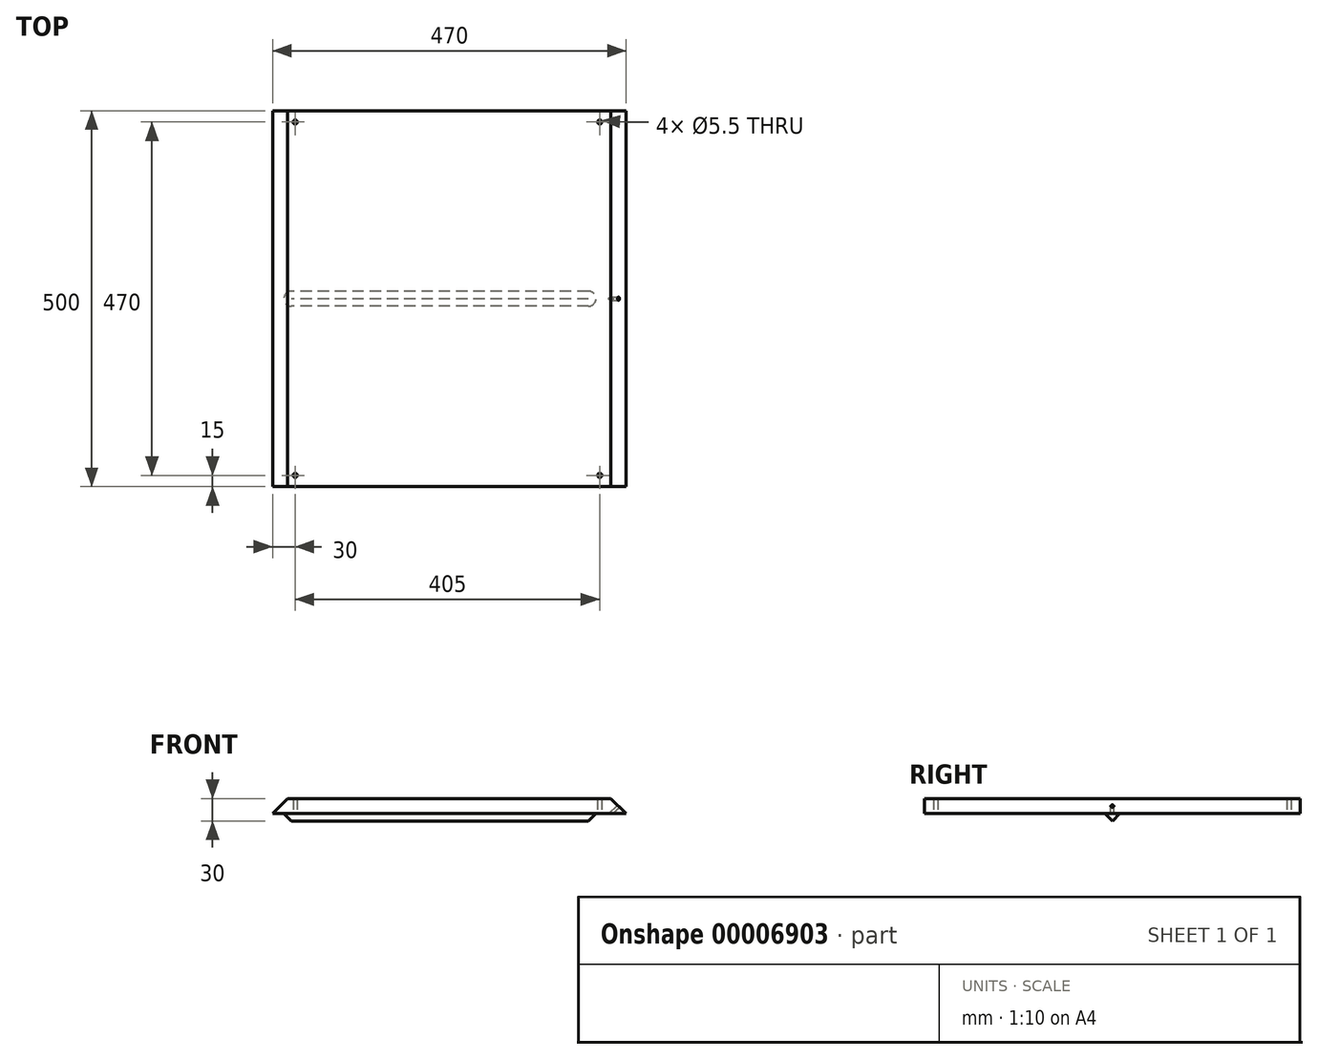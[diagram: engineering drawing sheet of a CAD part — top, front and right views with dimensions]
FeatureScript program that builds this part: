
annotation { "Feature Type Name" : "Feature", "Feature Type Description" : "" }
export const myFeature = defineFeature(function(context is Context, id is Id, definition is map)
    precondition{}
    {
        {
            var Q0;
            Q0=qCreatedBy(makeId("Top.planeOp"),FACE);
            var sketch = newSketch(context, id + "F0", { "sketchPlane" : qUnion([Q0])});
            skLineSegment(sketch, "E0.rect.bottom", {"start": v(242.5, -250) * mm, "end": v(-242.5, -250) * mm});
            skLineSegment(sketch, "E0.rect.top", {"start": v(242.5, 250) * mm, "end": v(-242.5, 250) * mm});
            skLineSegment(sketch, "E0.rect.left", {"start": v(242.5, -250) * mm, "end": v(242.5, 250) * mm});
            skLineSegment(sketch, "E0.rect.right", {"start": v(-242.5, -250) * mm, "end": v(-242.5, 250) * mm});
            skPoint(sketch, "E0.rect.middle", {"position": v(0, 0) * mm});
            skLineSegment(sketch, "E1", {"start": v(-242.5, 0) * mm, "end": v(242.5, 0) * mm, "construction": true});
            skCircle(sketch, "E2", {"center": v(-212.5, 235) * mm, "radius": 2.75 * mm});
            skCircle(sketch, "E3", {"center": v(-212.5, -235) * mm, "radius": 2.75 * mm});
            skCircle(sketch, "E4", {"center": v(192.5, 235) * mm, "radius": 2.75 * mm});
            skCircle(sketch, "E5", {"center": v(192.5, -235) * mm, "radius": 2.75 * mm});
            skSolve(sketch);
        }
        {
            var Q0;
            Q0=qSketchRegion(id+"F0",true);
            var Q1;
            Q1=makeQuery(id+"F0.imprint","IMPRINT",FACE,{"disambiguationData":[TD([[makeQuery(id+"F0.imprint","IMPRINT",EDGE,{"derivedFrom":sQuery(id+"F0.wireOp",EDGE,"E0.rect.bottom")}),-1.0]])]});
            extrude(context, id + "F1", {"entities" : qUnion([Q0, Q1]), "depth" : (30) * mm});
        }
        {
            var Q0;
            Q0=makeQuery(id+"F1.opExtrude","SWEPT_FACE",FACE,{"disambiguationData":[OSD([sQuery(id+"F0.wireOp",EDGE,"E0.rect.right")])]});
            var sketch = newSketch(context, id + "F2", { "sketchPlane" : qUnion([Q0])});
            skLineSegment(sketch, "E6", {"start": v(0, 0) * mm, "end": v(-10, 10) * mm});
            skLineSegment(sketch, "E7", {"start": v(0, 0) * mm, "end": v(10, 10) * mm});
            skLineSegment(sketch, "E8", {"start": v(-10, 10) * mm, "end": v(-250, 10) * mm});
            skLineSegment(sketch, "E9", {"start": v(10, 10) * mm, "end": v(250, 10) * mm});
            skSolve(sketch);
        }
        {
            var Q0;
            Q0=qSketchRegion(id+"F2",true);
            var Q1;
            {var subQ2=sQuery(id+"F2.wireOp",EDGE,"E6");Q1=makeQuery(id+"F2.imprint","IMPRINT",FACE,{"disambiguationData":[TD([[makeQuery(id+"F2.imprint","IMPRINT",EDGE,{"derivedFrom":subQ2}),1.0]])]});}
            var Q2;
            {var subQ2=sQuery(id+"F2.wireOp",EDGE,"E7");Q2=makeQuery(id+"F2.imprint","IMPRINT",FACE,{"disambiguationData":[TD([[makeQuery(id+"F2.imprint","IMPRINT",EDGE,{"derivedFrom":subQ2}),-1.0]])]});}
            extrude(context, id + "F3", {"entities" : qUnion([Q0, Q1, Q2]), "operationType" : NewBodyOperationType.REMOVE, "endBound" : BoundingType.THROUGH_ALL, "oppositeDirection" : true, "depth" : 25 * mm});
        }
        {
            var Q0;
            Q0=makeQuery(id+"F1.opExtrude","SWEPT_FACE",FACE,{"disambiguationData":[OSD([sQuery(id+"F0.wireOp",EDGE,"E0.rect.right")])]});
            var sketch = newSketch(context, id + "F4", { "sketchPlane" : qUnion([Q0])});
            skLineSegment(sketch, "E10", {"start": v(-10, 10) * mm, "end": v(10, 10) * mm});
            skSolve(sketch);
        }
        {
            var Q0;
            Q0=qSketchRegion(id+"F4",true);
            var Q1;
            Q1=makeQuery(id+"F4.imprint","IMPRINT",FACE,{"disambiguationData":[TD([[makeQuery(id+"F4.imprint","IMPRINT",EDGE,{"derivedFrom":sQuery(id+"F4.wireOp",EDGE,"E10")}),-1.0]])]});
            extrude(context, id + "F5", {"entities" : qUnion([Q0, Q1]), "operationType" : NewBodyOperationType.REMOVE, "oppositeDirection" : true, "depth" : 25 * mm});
        }
        {
            var Q0;
            Q0=makeQuery(id+"F5.boolean.opBoolean","COPY",FACE,{"derivedFrom":makeQuery(id+"F5.opExtrude","CAP_FACE",FACE,{"disambiguationData":[OSD([sQuery(id+"F2.wireOp",EDGE,"E6"),sQuery(id+"F2.wireOp",EDGE,"E7"),sQuery(id+"F4.wireOp",EDGE,"E10")])],"isStart":false})});
            var sketch = newSketch(context, id + "F6", { "sketchPlane" : qUnion([Q0])});
            skLineSegment(sketch, "E11", {"start": v(0, 0) * mm, "end": v(0, 10) * mm});
            skSolve(sketch);
        }
        {
            var Q0;
            {var subQ1=sQuery(id+"F6.wireOp",EDGE,"E11");Q0=makeQuery(id+"F6.imprint","IMPRINT",FACE,{"disambiguationData":[TD([[makeQuery(id+"F6.imprint","IMPRINT",EDGE,{"derivedFrom":subQ1}),1.0]])]});}
            var Q1;
            Q1=sQuery(id+"F6.wireOp",EDGE,"E11");
            revolve(context, id + "F7", {"operationType" : NewBodyOperationType.ADD, "entities" : qUnion([Q0]), "axis" : qUnion([Q1]), "revolveType" : RevolveType.FULL});
        }
        {
            var Q0;
            Q0=makeQuery(id+"F1.opExtrude","SWEPT_FACE",FACE,{"disambiguationData":[OSD([sQuery(id+"F0.wireOp",EDGE,"E0.rect.top")])]});
            var sketch = newSketch(context, id + "F8", { "sketchPlane" : qUnion([Q0])});
            skLineSegment(sketch, "E12", {"start": v(242.5, 10) * mm, "end": v(222.5, 30) * mm});
            skSolve(sketch);
        }
        {
            var Q0;
            Q0=qSketchRegion(id+"F8",true);
            var Q1;
            {var subQ2=sQuery(id+"F8.wireOp",EDGE,"E12");Q1=makeQuery(id+"F8.imprint","IMPRINT",FACE,{"disambiguationData":[TD([[makeQuery(id+"F8.imprint","IMPRINT",EDGE,{"derivedFrom":subQ2}),-1.0]])]});}
            extrude(context, id + "F9", {"entities" : qUnion([Q0, Q1]), "operationType" : NewBodyOperationType.REMOVE, "endBound" : BoundingType.THROUGH_ALL, "oppositeDirection" : true, "depth" : 25 * mm});
        }
        {
            var Q0;
            Q0=makeQuery(id+"F1.opExtrude","SWEPT_FACE",FACE,{"disambiguationData":[OSD([sQuery(id+"F0.wireOp",EDGE,"E0.rect.left")])]});
            extrude(context, id + "F10", {"entities" : qUnion([Q0]), "operationType" : NewBodyOperationType.REMOVE, "oppositeDirection" : true, "depth" : (15) * mm});
        }
        {
            var Q0;
            Q0=makeQuery(id+"F10.boolean.opBoolean","COPY",FACE,{"derivedFrom":makeQuery(id+"F10.opExtrude","CAP_FACE",FACE,{"disambiguationData":[OSD([sQuery(id+"F0.wireOp",EDGE,"E0.rect.left")])],"isStart":false})});
            var sketch = newSketch(context, id + "F11", { "sketchPlane" : qUnion([Q0])});
            skLineSegment(sketch, "E13", {"start": v(-10, 10) * mm, "end": v(10, 10) * mm});
            skSolve(sketch);
        }
        {
            var Q0;
            Q0=makeQuery(id+"F11.imprint","IMPRINT",FACE,{"disambiguationData":[TD([[makeQuery(id+"F11.imprint","IMPRINT",EDGE,{"derivedFrom":sQuery(id+"F11.wireOp",EDGE,"E13")}),-1.0]])]});
            extrude(context, id + "F12", {"entities" : qUnion([Q0]), "operationType" : NewBodyOperationType.REMOVE, "oppositeDirection" : true, "depth" : (50) * mm});
        }
        {
            var Q0;
            Q0=makeQuery(id+"F12.boolean.opBoolean","COPY",FACE,{"derivedFrom":makeQuery(id+"F12.opExtrude","CAP_FACE",FACE,{"disambiguationData":[OSD([sQuery(id+"F0.wireOp",EDGE,"E0.rect.left"),sQuery(id+"F2.wireOp",EDGE,"E6"),sQuery(id+"F2.wireOp",EDGE,"E7"),sQuery(id+"F11.wireOp",EDGE,"E13")])],"isStart":false})});
            var sketch = newSketch(context, id + "F13", { "sketchPlane" : qUnion([Q0])});
            skLineSegment(sketch, "E14", {"start": v(0, 0) * mm, "end": v(0, 10) * mm});
            skSolve(sketch);
        }
        {
            var Q0;
            {var subQ1=sQuery(id+"F13.wireOp",EDGE,"E14");Q0=makeQuery(id+"F13.imprint","IMPRINT",FACE,{"disambiguationData":[TD([[makeQuery(id+"F13.imprint","IMPRINT",EDGE,{"derivedFrom":subQ1}),-1.0]])]});}
            var Q1;
            Q1=sQuery(id+"F13.wireOp",EDGE,"E14");
            revolve(context, id + "F14", {"operationType" : NewBodyOperationType.ADD, "entities" : qUnion([Q0]), "axis" : qUnion([Q1]), "revolveType" : RevolveType.FULL});
        }
        {
            var Q0;
            Q0=makeQuery(id+"F1.opExtrude","SWEPT_FACE",FACE,{"disambiguationData":[OSD([sQuery(id+"F0.wireOp",EDGE,"E0.rect.top")])]});
            var sketch = newSketch(context, id + "F15", { "sketchPlane" : qUnion([Q0])});
            skLineSegment(sketch, "E15", {"start": v(-227.5, 10) * mm, "end": v(-207.5, 30) * mm});
            skSolve(sketch);
        }
        {
            var Q0;
            Q0=qSketchRegion(id+"F15",true);
            var Q1;
            {var subQ2=sQuery(id+"F15.wireOp",EDGE,"E15");Q1=makeQuery(id+"F15.imprint","IMPRINT",FACE,{"disambiguationData":[TD([[makeQuery(id+"F15.imprint","IMPRINT",EDGE,{"derivedFrom":subQ2}),1.0]])]});}
            extrude(context, id + "F16", {"entities" : qUnion([Q0, Q1]), "operationType" : NewBodyOperationType.REMOVE, "endBound" : BoundingType.THROUGH_ALL, "oppositeDirection" : true, "depth" : 25 * mm});
        }
        {
            var Q0;
            Q0=makeQuery(id+"F16.boolean.opBoolean","COPY",FACE,{"derivedFrom":makeQuery(id+"F16.opExtrude","SWEPT_FACE",FACE,{"disambiguationData":[OSD([sQuery(id+"F15.wireOp",EDGE,"E15")])]})});
            var sketch = newSketch(context, id + "F17", { "sketchPlane" : qUnion([Q0])});
            skLineSegment(sketch, "E16", {"start": v(0, -125.51) * mm, "end": v(0, -153.8) * mm, "construction": true});
            skCircle(sketch, "E17", {"center": v(0, -139.65) * mm, "radius": 2 * mm});
            skSolve(sketch);
        }
        {
            var Q0;
            Q0=qSketchRegion(id+"F17",true);
            extrude(context, id + "F18", {"entities" : qUnion([Q0]), "operationType" : NewBodyOperationType.REMOVE, "endBound" : BoundingType.THROUGH_ALL, "oppositeDirection" : true, "depth" : 25 * mm});
        }
    });
